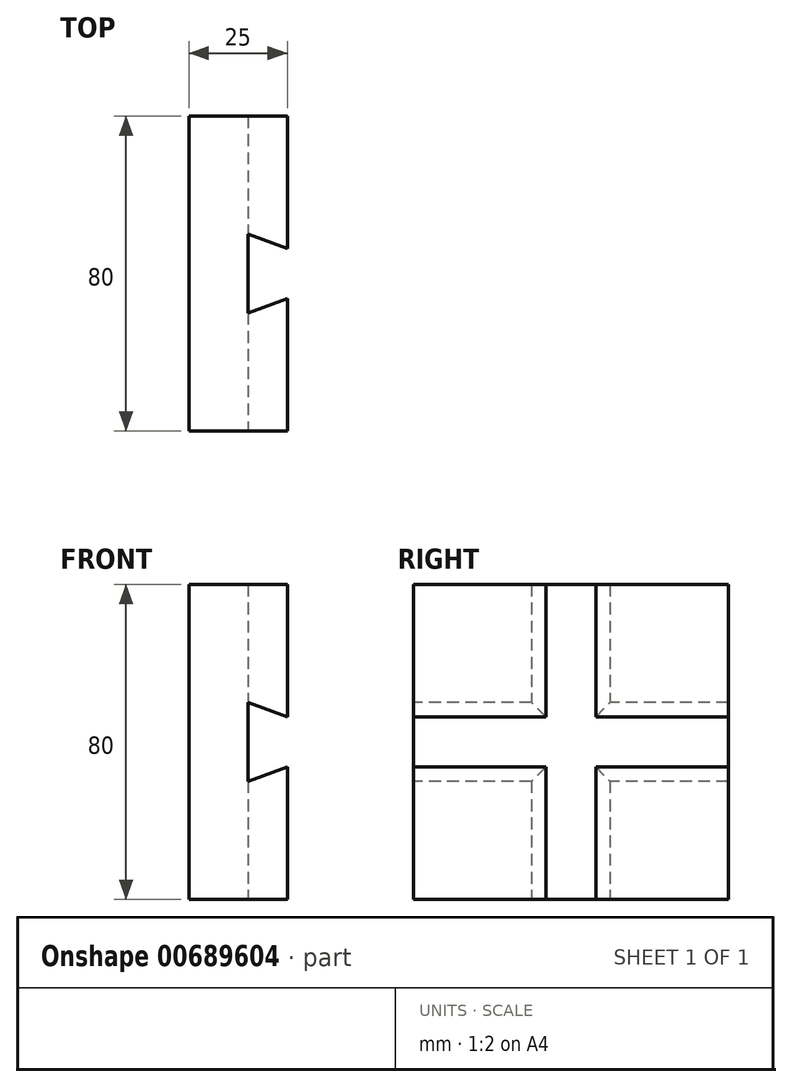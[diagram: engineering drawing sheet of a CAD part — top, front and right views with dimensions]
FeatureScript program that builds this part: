
annotation { "Feature Type Name" : "Feature", "Feature Type Description" : "" }
export const myFeature = defineFeature(function(context is Context, id is Id, definition is map)
    precondition{}
    {
        {
            var Q0;
            Q0=qCreatedBy(makeId("Right.planeOp"),FACE);
            var sketch = newSketch(context, id + "F0", { "sketchPlane" : qUnion([Q0])});
            skLineSegment(sketch, "E0.bottom", {"start": v(0, 0) * mm, "end": v(-80, 0) * mm});
            skLineSegment(sketch, "E0.top", {"start": v(0, 80) * mm, "end": v(-80, 80) * mm});
            skLineSegment(sketch, "E0.left", {"start": v(0, 0) * mm, "end": v(0, 80) * mm});
            skLineSegment(sketch, "E0.right", {"start": v(-80, 0) * mm, "end": v(-80, 80) * mm});
            skSolve(sketch);
        }
        {
            var Q0;
            Q0=makeQuery(id+"F0.imprint","IMPRINT",FACE,{"disambiguationData":[TD([[makeQuery(id+"F0.imprint","IMPRINT",EDGE,{"derivedFrom":sQuery(id+"F0.wireOp",EDGE,"E0.bottom")}),-1.0]])]});
            extrude(context, id + "F1", {"entities" : qUnion([Q0]), "depth" : 25 * mm, "offsetDistance" : 25 * mm});
        }
        {
            var Q0;
            Q0=makeQuery(id+"F1.opExtrude","SWEPT_FACE",FACE,{"disambiguationData":[OSD([sQuery(id+"F0.wireOp",EDGE,"E0.bottom")])]});
            var sketch = newSketch(context, id + "F2", { "sketchPlane" : qUnion([Q0])});
            skLineSegment(sketch, "E1.left", {"start": v(15, 50) * mm, "end": v(15, 30) * mm});
            skPoint(sketch, "E1.middle", {"position": v(25, 40) * mm});
            skLineSegment(sketch, "E2", {"start": v(25, 40) * mm, "end": v(25, 33.64) * mm});
            skLineSegment(sketch, "E3", {"start": v(25, 33.64) * mm, "end": v(15, 30) * mm});
            skLineSegment(sketch, "E4", {"start": v(25, 40) * mm, "end": v(25, 46.36) * mm});
            skLineSegment(sketch, "E5", {"start": v(25, 46.36) * mm, "end": v(15, 50) * mm});
            skPoint(sketch, "E1.top.end.orphan", {"position": v(35, 30) * mm});
            skPoint(sketch, "E1.bottom.end.orphan", {"position": v(35, 50) * mm});
            skSolve(sketch);
        }
        {
            var Q0;
            Q0=makeQuery(id+"F2.imprint","IMPRINT",FACE,{"disambiguationData":[TD([[makeQuery(id+"F2.imprint","IMPRINT",EDGE,{"derivedFrom":sQuery(id+"F2.wireOp",EDGE,"E1.left")}),1.0]])]});
            extrude(context, id + "F3", {"entities" : qUnion([Q0]), "operationType" : NewBodyOperationType.REMOVE, "oppositeDirection" : true, "depth" : 80 * mm, "offsetDistance" : 25 * mm});
        }
        {
            var Q0;
            Q0=makeQuery(id+"F1.opExtrude","SWEPT_FACE",FACE,{"disambiguationData":[OSD([sQuery(id+"F0.wireOp",EDGE,"E0.right")])]});
            var sketch = newSketch(context, id + "F4", { "sketchPlane" : qUnion([Q0])});
            skLineSegment(sketch, "E6.left", {"start": v(15, 30) * mm, "end": v(15, 50) * mm});
            skPoint(sketch, "E6.middle", {"position": v(25, 40) * mm});
            skLineSegment(sketch, "E7", {"start": v(25, 40) * mm, "end": v(25, 33.64) * mm});
            skLineSegment(sketch, "E8", {"start": v(25, 33.64) * mm, "end": v(15, 30) * mm});
            skLineSegment(sketch, "E9", {"start": v(25, 40) * mm, "end": v(25, 46.36) * mm});
            skLineSegment(sketch, "E10", {"start": v(25, 46.36) * mm, "end": v(15, 50) * mm});
            skPoint(sketch, "E6.top.end.orphan", {"position": v(35, 50) * mm});
            skPoint(sketch, "E6.bottom.end.orphan", {"position": v(35, 30) * mm});
            skSolve(sketch);
        }
        {
            var Q0;
            Q0=makeQuery(id+"F4.imprint","IMPRINT",FACE,{"disambiguationData":[TD([[makeQuery(id+"F4.imprint","IMPRINT",EDGE,{"derivedFrom":sQuery(id+"F4.wireOp",EDGE,"E6.left")}),-1.0]])]});
            extrude(context, id + "F5", {"entities" : qUnion([Q0]), "operationType" : NewBodyOperationType.REMOVE, "oppositeDirection" : true, "depth" : 80 * mm, "offsetDistance" : 25 * mm});
        }
    });
